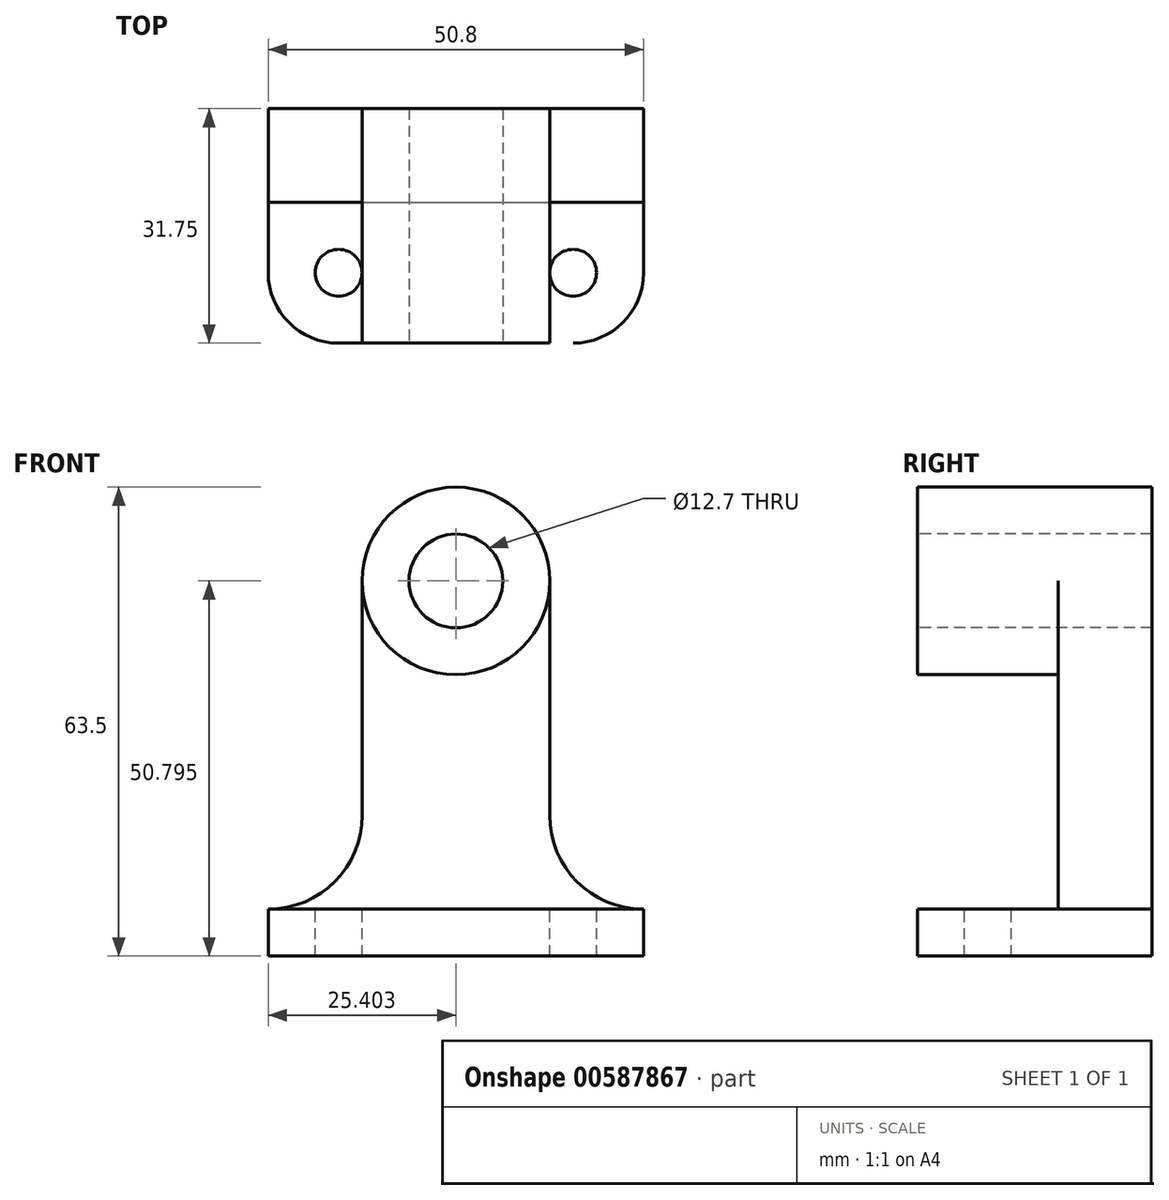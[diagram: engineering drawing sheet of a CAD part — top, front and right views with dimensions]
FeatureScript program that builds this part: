
annotation { "Feature Type Name" : "Feature", "Feature Type Description" : "" }
export const myFeature = defineFeature(function(context is Context, id is Id, definition is map)
    precondition{}
    {
        {
            var Q0;
            Q0=qCreatedBy(makeId("Front.planeOp"),FACE);
            var sketch = newSketch(context, id + "F0", { "sketchPlane" : qUnion([Q0])});
            skLineSegment(sketch, "E0.bottom", {"start": v(-69.24, 69.97) * mm, "end": v(-18.44, 69.97) * mm});
            skLineSegment(sketch, "E0.top", {"start": v(-69.24, 6.47) * mm, "end": v(-18.44, 6.47) * mm});
            skLineSegment(sketch, "E0.left", {"start": v(-69.24, 69.97) * mm, "end": v(-69.24, 6.47) * mm});
            skLineSegment(sketch, "E0.right", {"start": v(-18.44, 69.97) * mm, "end": v(-18.44, 6.47) * mm});
            skSolve(sketch);
        }
        {
            var Q0;
            Q0 = qSketchRegion(id + "F0", true);
            extrude(context, id + "F1", {"entities" : qUnion([Q0]), "depth" : 31.75 * mm, "offsetDistance" : 25.4 * mm});
        }
        {
            var Q0;
            Q0=makeQuery(id+"F1.opExtrude","CAP_FACE",FACE,{"disambiguationData":[OSD([sQuery(id+"F0.wireOp",EDGE,"E0.bottom"),sQuery(id+"F0.wireOp",EDGE,"E0.top"),sQuery(id+"F0.wireOp",EDGE,"E0.left"),sQuery(id+"F0.wireOp",EDGE,"E0.right")])],"isStart":true});
            var sketch = newSketch(context, id + "F2", { "sketchPlane" : qUnion([Q0])});
            skLineSegment(sketch, "E1", {"start": v(18.44, 12.82) * mm, "end": v(69.24, 12.82) * mm});
            skArc(sketch, "E2", {"start": v(56.54, 57.27) * mm, "mid": v(43.84, 69.97) * mm, "end": v(31.14, 57.27) * mm});
            skArc(sketch, "E3", {"start": v(18.44, 12.82) * mm, "mid": v(27.42, 16.53) * mm, "end": v(31.14, 25.52) * mm});
            skArc(sketch, "E4", {"start": v(56.54, 25.52) * mm, "mid": v(60.26, 16.53) * mm, "end": v(69.24, 12.82) * mm});
            skLineSegment(sketch, "E5", {"start": v(31.14, 57.27) * mm, "end": v(31.14, 25.52) * mm});
            skLineSegment(sketch, "E6", {"start": v(56.54, 57.27) * mm, "end": v(56.54, 25.52) * mm});
            skSolve(sketch);
        }
        {
            var Q0;
            {var subQ6=sQuery(id+"F2.wireOp",EDGE,"E3");Q0=makeQuery(id+"F2.imprint","IMPRINT",FACE,{"disambiguationData":[TD([[makeQuery(id+"F2.imprint","IMPRINT",EDGE,{"derivedFrom":subQ6}),1.0]])]});}
            var Q1;
            {var subQ5=sQuery(id+"F2.wireOp",EDGE,"E4");Q1=makeQuery(id+"F2.imprint","IMPRINT",FACE,{"disambiguationData":[TD([[makeQuery(id+"F2.imprint","IMPRINT",EDGE,{"derivedFrom":subQ5}),1.0]])]});}
            extrude(context, id + "F3", {"entities" : qUnion([Q0, Q1]), "operationType" : NewBodyOperationType.REMOVE, "endBound" : BoundingType.THROUGH_ALL, "oppositeDirection" : true, "depth" : 25.4 * mm, "offsetDistance" : 25.4 * mm});
        }
        {
            var Q0;
            Q0=makeQuery(id+"F1.opExtrude","CAP_FACE",FACE,{"disambiguationData":[OSD([sQuery(id+"F0.wireOp",EDGE,"E0.bottom"),sQuery(id+"F0.wireOp",EDGE,"E0.top"),sQuery(id+"F0.wireOp",EDGE,"E0.left"),sQuery(id+"F0.wireOp",EDGE,"E0.right")])],"isStart":false});
            var sketch = newSketch(context, id + "F4", { "sketchPlane" : qUnion([Q0])});
            skLineSegment(sketch, "E7", {"start": v(-69.24, 12.82) * mm, "end": v(-18.44, 12.82) * mm});
            skArc(sketch, "E8", {"start": v(-69.24, 12.82) * mm, "mid": v(-60.26, 16.53) * mm, "end": v(-56.54, 25.52) * mm});
            skArc(sketch, "E9", {"start": v(-31.14, 25.52) * mm, "mid": v(-27.42, 16.53) * mm, "end": v(-18.44, 12.82) * mm});
            skArc(sketch, "E10", {"start": v(-56.54, 57.27) * mm, "mid": v(-43.84, 44.57) * mm, "end": v(-31.14, 57.27) * mm});
            skLineSegment(sketch, "E11", {"start": v(-56.54, 57.27) * mm, "end": v(-56.54, 25.52) * mm});
            skLineSegment(sketch, "E12", {"start": v(-31.14, 57.27) * mm, "end": v(-31.14, 25.52) * mm});
            skSolve(sketch);
        }
        {
            var Q0;
            Q0 = qSketchRegion(id + "F4", true);
            extrude(context, id + "F5", {"entities" : qUnion([Q0]), "operationType" : NewBodyOperationType.REMOVE, "oppositeDirection" : true, "depth" : 19.05 * mm, "offsetDistance" : 25.4 * mm});
        }
        {
            var Q0;
            Q0=makeQuery(id+"F5.boolean.opBoolean","COPY",FACE,{"derivedFrom":makeQuery(id+"F5.opExtrude","SWEPT_FACE",FACE,{"disambiguationData":[OSD([sQuery(id+"F4.wireOp",EDGE,"E7")])]})});
            var sketch = newSketch(context, id + "F6", { "sketchPlane" : qUnion([Q0])});
            skCircle(sketch, "E13", {"center": v(-27.96, -22.23) * mm, "radius": 3.18 * mm});
            skArc(sketch, "E14", {"start": v(-27.96, -31.75) * mm, "mid": v(-21.23, -28.96) * mm, "end": v(-18.44, -22.23) * mm});
            skCircle(sketch, "E15", {"center": v(-59.71, -22.23) * mm, "radius": 3.18 * mm});
            skArc(sketch, "E16", {"start": v(-69.24, -22.23) * mm, "mid": v(-66.45, -28.96) * mm, "end": v(-59.71, -31.75) * mm});
            skSolve(sketch);
        }
        {
            var Q0;
            Q0 = qSketchRegion(id + "F6", true);
            var Q1;
            {var subQ0=sQuery(id+"F6.wireOp",EDGE,"E16");Q1=makeQuery(id+"F6.imprint","IMPRINT",FACE,{"disambiguationData":[TD([[makeQuery(id+"F6.imprint","IMPRINT",EDGE,{"derivedFrom":subQ0}),-1.0]])]});}
            var Q2;
            {var subQ0=sQuery(id+"F6.wireOp",EDGE,"E14");Q2=makeQuery(id+"F6.imprint","IMPRINT",FACE,{"disambiguationData":[TD([[makeQuery(id+"F6.imprint","IMPRINT",EDGE,{"derivedFrom":subQ0}),-1.0]])]});}
            extrude(context, id + "F7", {"entities" : qUnion([Q0, Q1, Q2]), "operationType" : NewBodyOperationType.REMOVE, "oppositeDirection" : true, "depth" : 25.4 * mm, "offsetDistance" : 25.4 * mm});
        }
        {
            var Q0;
            {var subQ1=sQuery(id+"F0.wireOp",EDGE,"E0.bottom");Q0=makeQuery(id+"F5.boolean.opBoolean","SPLIT",FACE,{"disambiguationData":[TD([makeQuery(id+"F5.opExtrude","SWEPT_FACE",FACE,{"disambiguationData":[OSD([sQuery(id+"F4.wireOp",EDGE,"E10")])]})])],"derivedFrom":makeQuery(id+"F1.opExtrude","CAP_FACE",FACE,{"disambiguationData":[OSD([subQ1,sQuery(id+"F0.wireOp",EDGE,"E0.top"),sQuery(id+"F0.wireOp",EDGE,"E0.left"),sQuery(id+"F0.wireOp",EDGE,"E0.right")])],"isStart":false})});}
            var sketch = newSketch(context, id + "F8", { "sketchPlane" : qUnion([Q0])});
            skCircle(sketch, "E17", {"center": v(-43.84, 57.27) * mm, "radius": 6.35 * mm});
            skSolve(sketch);
        }
        {
            var Q0;
            Q0 = qSketchRegion(id + "F8", true);
            extrude(context, id + "F9", {"entities" : qUnion([Q0]), "operationType" : NewBodyOperationType.REMOVE, "endBound" : BoundingType.THROUGH_ALL, "oppositeDirection" : true, "depth" : 25.4 * mm, "offsetDistance" : 25.4 * mm});
        }
    });
